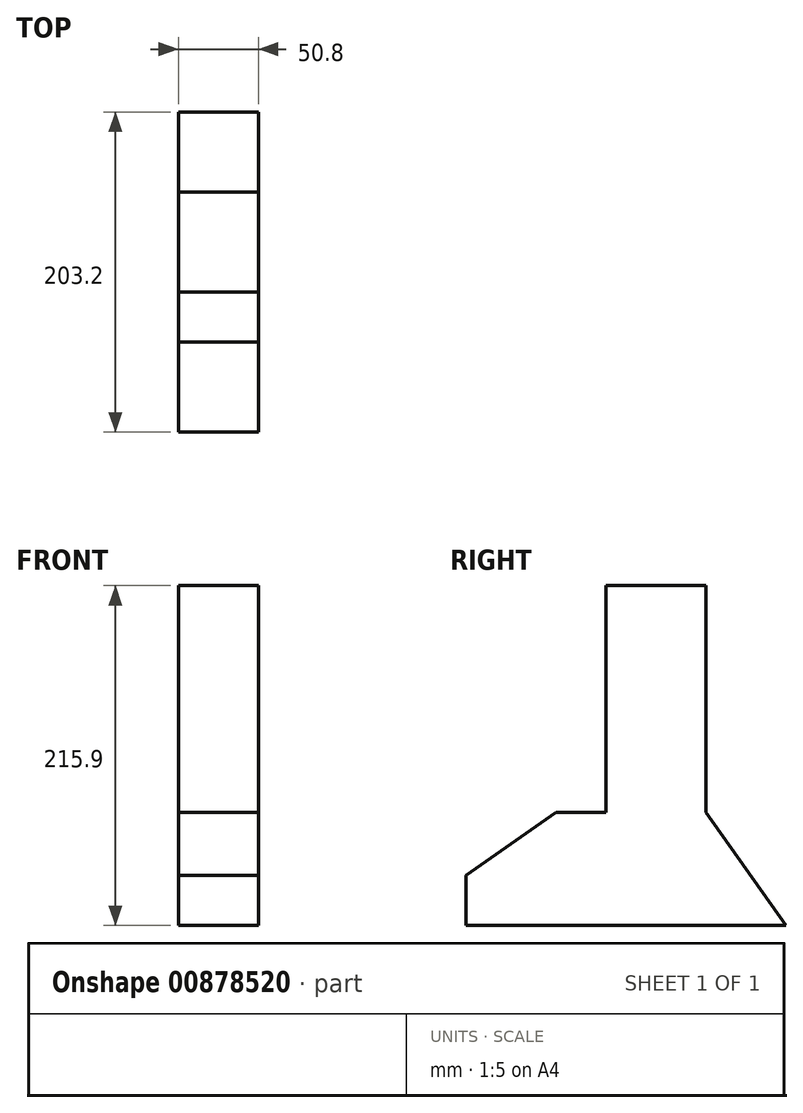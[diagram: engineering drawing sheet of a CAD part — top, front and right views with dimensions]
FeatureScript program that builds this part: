
annotation { "Feature Type Name" : "Feature", "Feature Type Description" : "" }
export const myFeature = defineFeature(function(context is Context, id is Id, definition is map)
    precondition{}
    {
        {
            var Q0;
            Q0=qCreatedBy(makeId("Right.planeOp"),FACE);
            var sketch = newSketch(context, id + "F0", { "sketchPlane" : qUnion([Q0])});
            skLineSegment(sketch, "E0", {"start": v(0, 0) * mm, "end": v(0, 31.75) * mm});
            skLineSegment(sketch, "E1", {"start": v(0, 31.75) * mm, "end": v(57.22, 71.81) * mm});
            skLineSegment(sketch, "E2", {"start": v(57.22, 71.81) * mm, "end": v(152.4, 71.81) * mm});
            skLineSegment(sketch, "E3", {"start": v(152.4, 71.81) * mm, "end": v(152.4, 0) * mm});
            skLineSegment(sketch, "E4", {"start": v(152.4, 0) * mm, "end": v(0, 0) * mm});
            skLineSegment(sketch, "E5", {"start": v(152.4, 71.81) * mm, "end": v(203.2, 0) * mm});
            skLineSegment(sketch, "E6", {"start": v(203.2, 0) * mm, "end": v(152.4, 0) * mm});
            skLineSegment(sketch, "E7.bottom", {"start": v(88.9, 71.81) * mm, "end": v(152.4, 71.81) * mm});
            skLineSegment(sketch, "E7.top", {"start": v(88.9, 215.9) * mm, "end": v(152.4, 215.9) * mm});
            skLineSegment(sketch, "E7.left", {"start": v(88.9, 71.81) * mm, "end": v(88.9, 215.9) * mm});
            skLineSegment(sketch, "E7.right", {"start": v(152.4, 71.81) * mm, "end": v(152.4, 215.9) * mm});
            skSolve(sketch);
        }
        {
            var Q0;
            Q0 = qSketchRegion(id + "F0", true);
            extrude(context, id + "F1", {"entities" : qUnion([Q0]), "endBound" : BoundingType.SYMMETRIC, "depth" : 50.8 * mm, "offsetDistance" : 25.4 * mm});
        }
    });
